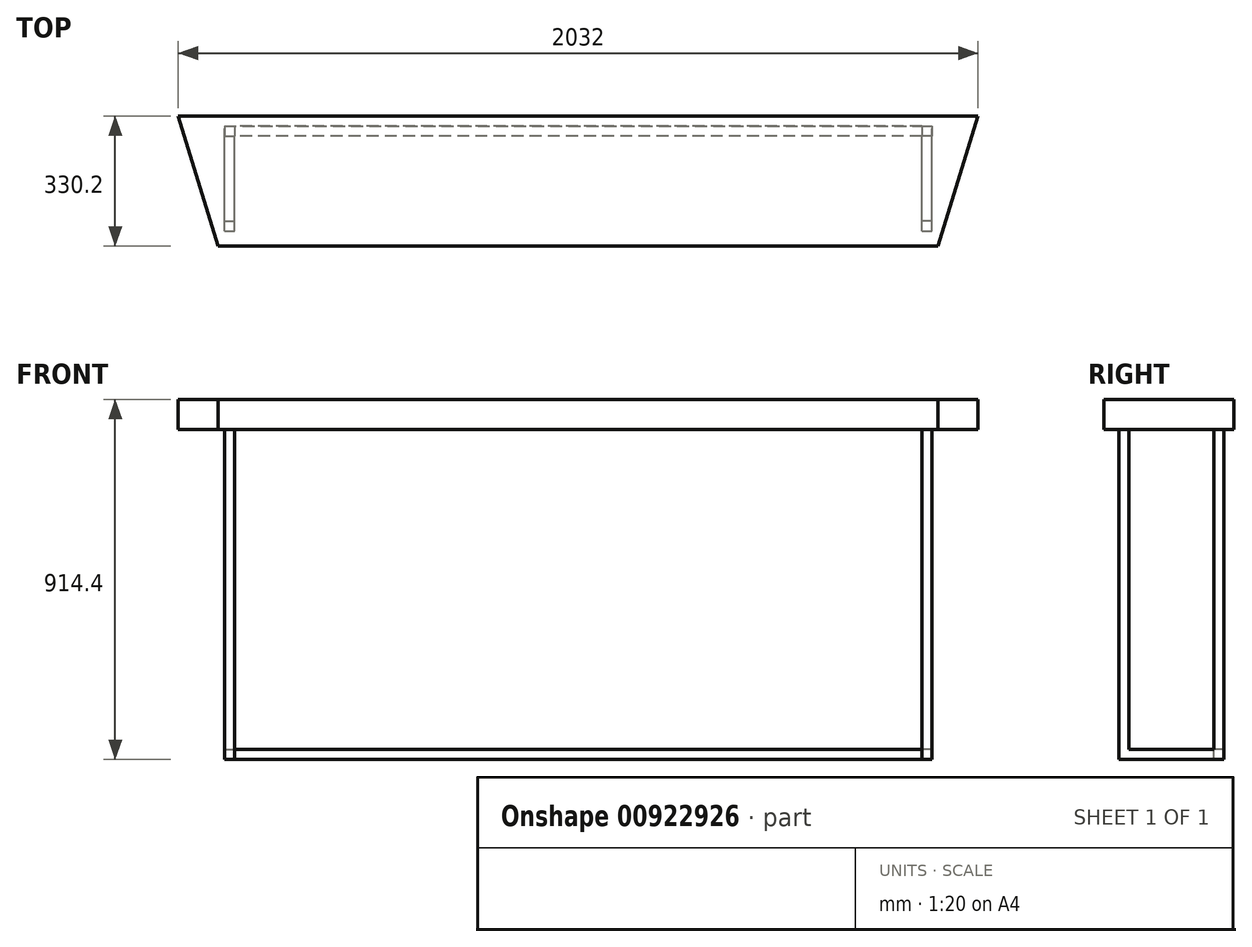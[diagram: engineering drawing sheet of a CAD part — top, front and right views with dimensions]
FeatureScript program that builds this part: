
annotation { "Feature Type Name" : "Feature", "Feature Type Description" : "" }
export const myFeature = defineFeature(function(context is Context, id is Id, definition is map)
    precondition{}
    {
        {
            var Q0;
            Q0=qCreatedBy(makeId("Top.planeOp"),FACE);
            var sketch = newSketch(context, id + "F0", { "sketchPlane" : qUnion([Q0])});
            skLineSegment(sketch, "E0.bottom", {"start": v(-914.4, 165.1) * mm, "end": v(914.4, 165.1) * mm});
            skLineSegment(sketch, "E0.top", {"start": v(-914.4, -165.1) * mm, "end": v(914.4, -165.1) * mm});
            skLineSegment(sketch, "E0.left", {"start": v(-914.4, 165.1) * mm, "end": v(-914.4, -165.1) * mm});
            skLineSegment(sketch, "E0.right", {"start": v(914.4, 165.1) * mm, "end": v(914.4, -165.1) * mm});
            skPoint(sketch, "E0.middle", {"position": v(0, 0) * mm});
            skLineSegment(sketch, "E1.bottom", {"start": v(-1016, 165.1) * mm, "end": v(1016, 165.1) * mm});
            skLineSegment(sketch, "E1.top", {"start": v(-1016, -165.1) * mm, "end": v(1016, -165.1) * mm});
            skLineSegment(sketch, "E1.left", {"start": v(-1016, 165.1) * mm, "end": v(-1016, -165.1) * mm});
            skLineSegment(sketch, "E1.right", {"start": v(1016, 165.1) * mm, "end": v(1016, -165.1) * mm});
            skLineSegment(sketch, "E2", {"start": v(-1016, 165.1) * mm, "end": v(-914.4, -165.1) * mm});
            skLineSegment(sketch, "E3", {"start": v(914.4, -165.1) * mm, "end": v(1016, 165.1) * mm});
            skSolve(sketch);
        }
        {
            var Q0;
            {var subQ0=sQuery(id+"F0.wireOp",EDGE,"E0.left");Q0=makeQuery(id+"F0.imprint","IMPRINT",FACE,{"disambiguationData":[TD([[makeQuery(id+"F0.imprint","IMPRINT",EDGE,{"derivedFrom":subQ0}),1.0]])]});}
            var Q1;
            {var subQ0=sQuery(id+"F0.wireOp",EDGE,"E0.left");Q1=makeQuery(id+"F0.imprint","IMPRINT",FACE,{"disambiguationData":[TD([[makeQuery(id+"F0.imprint","IMPRINT",EDGE,{"derivedFrom":subQ0}),-1.0]])]});}
            var Q2;
            {var subQ0=sQuery(id+"F0.wireOp",EDGE,"E0.right");Q2=makeQuery(id+"F0.imprint","IMPRINT",FACE,{"disambiguationData":[TD([[makeQuery(id+"F0.imprint","IMPRINT",EDGE,{"derivedFrom":subQ0}),1.0]])]});}
            extrude(context, id + "F1", {"entities" : qUnion([Q0, Q1, Q2]), "depth" : 76.2 * mm, "offsetDistance" : 25.4 * mm});
        }
        {
            var Q0;
            Q0=makeQuery(id+"F1.opExtrude","CAP_FACE",FACE,{"disambiguationData":[OSD([sQuery(id+"F0.wireOp",EDGE,"E1.bottom"),sQuery(id+"F0.wireOp",EDGE,"E1.top"),sQuery(id+"F0.wireOp",EDGE,"E2"),sQuery(id+"F0.wireOp",EDGE,"E3")])],"isStart":true});
            var sketch = newSketch(context, id + "F2", { "sketchPlane" : qUnion([Q0])});
            skLineSegment(sketch, "E4", {"start": v(-898.53, 127) * mm, "end": v(898.53, 127) * mm});
            skPoint(sketch, "E5", {"position": v(0, 127) * mm});
            skLineSegment(sketch, "E6.0", {"start": v(-898.52, -139.7) * mm, "end": v(898.53, -139.7) * mm});
            skLineSegment(sketch, "E7.bottom", {"start": v(-898.53, 127) * mm, "end": v(-873.13, 127) * mm});
            skLineSegment(sketch, "E7.top", {"start": v(-898.53, 101.6) * mm, "end": v(-873.13, 101.6) * mm});
            skLineSegment(sketch, "E7.left", {"start": v(-898.53, 127) * mm, "end": v(-898.53, 101.6) * mm});
            skLineSegment(sketch, "E7.right", {"start": v(-873.13, 127) * mm, "end": v(-873.13, 101.6) * mm});
            skLineSegment(sketch, "E8.bottom", {"start": v(-898.52, -139.7) * mm, "end": v(-873.12, -139.7) * mm});
            skLineSegment(sketch, "E8.top", {"start": v(-898.52, -114.3) * mm, "end": v(-873.12, -114.3) * mm});
            skLineSegment(sketch, "E8.left", {"start": v(-898.52, -139.7) * mm, "end": v(-898.52, -114.3) * mm});
            skLineSegment(sketch, "E8.right", {"start": v(-873.12, -139.7) * mm, "end": v(-873.12, -114.3) * mm});
            skLineSegment(sketch, "E9.bottom", {"start": v(898.53, 127) * mm, "end": v(873.13, 127) * mm});
            skLineSegment(sketch, "E9.top", {"start": v(898.53, 101.6) * mm, "end": v(873.13, 101.6) * mm});
            skLineSegment(sketch, "E9.left", {"start": v(898.53, 127) * mm, "end": v(898.53, 101.6) * mm});
            skLineSegment(sketch, "E9.right", {"start": v(873.13, 127) * mm, "end": v(873.13, 101.6) * mm});
            skLineSegment(sketch, "E10.bottom", {"start": v(898.53, -139.7) * mm, "end": v(873.13, -139.7) * mm});
            skLineSegment(sketch, "E10.top", {"start": v(898.53, -114.3) * mm, "end": v(873.13, -114.3) * mm});
            skLineSegment(sketch, "E10.left", {"start": v(898.53, -139.7) * mm, "end": v(898.53, -114.3) * mm});
            skLineSegment(sketch, "E10.right", {"start": v(873.13, -139.7) * mm, "end": v(873.13, -114.3) * mm});
            skSolve(sketch);
        }
        {
            var Q0;
            Q0 = qSketchRegion(id + "F2", true);
            extrude(context, id + "F3", {"entities" : qUnion([Q0]), "operationType" : NewBodyOperationType.ADD, "depth" : 838.2 * mm, "offsetDistance" : 25.4 * mm});
        }
        {
            var Q0;
            Q0=makeQuery(id+"F3.opExtrude","SWEPT_FACE",FACE,{"disambiguationData":[OSD([sQuery(id+"F2.wireOp",EDGE,"E8.right")])]});
            var sketch = newSketch(context, id + "F4", { "sketchPlane" : qUnion([Q0])});
            skLineSegment(sketch, "E11.0", {"start": v(114.3, -838.2) * mm, "end": v(114.3, 0) * mm});
            skLineSegment(sketch, "E12.0", {"start": v(139.7, -838.2) * mm, "end": v(139.7, 0) * mm});
            skLineSegment(sketch, "E13.0", {"start": v(139.7, -838.2) * mm, "end": v(114.3, -838.2) * mm});
            skLineSegment(sketch, "E14.0", {"start": v(139.7, -812.8) * mm, "end": v(114.3, -812.8) * mm});
            skSolve(sketch);
        }
        {
            var Q0;
            {var subQ0=sQuery(id+"F4.wireOp",EDGE,"E13.0");Q0=makeQuery(id+"F4.imprint","IMPRINT",FACE,{"disambiguationData":[TD([[makeQuery(id+"F4.imprint","IMPRINT",EDGE,{"derivedFrom":subQ0}),-1.0]])]});}
            extrude(context, id + "F5", {"entities" : qUnion([Q0]), "operationType" : NewBodyOperationType.ADD, "endBound" : BoundingType.UP_TO_NEXT, "depth" : 25.4 * mm, "offsetDistance" : 25.4 * mm});
        }
        {
            var Q0;
            Q0=makeQuery(id+"F5.boolean.opBoolean","MERGE",FACE,{"derivedFrom":[makeQuery(id+"F3.opExtrude","SWEPT_FACE",FACE,{"disambiguationData":[OSD([sQuery(id+"F2.wireOp",EDGE,"E8.top")])]}),makeQuery(id+"F3.opExtrude","SWEPT_FACE",FACE,{"disambiguationData":[OSD([sQuery(id+"F2.wireOp",EDGE,"E10.top")])]}),makeQuery(id+"F5.opExtrude","SWEPT_FACE",FACE,{"disambiguationData":[OSD([sQuery(id+"F4.wireOp",EDGE,"E11.0")])]})]});
            var sketch = newSketch(context, id + "F6", { "sketchPlane" : qUnion([Q0])});
            skLineSegment(sketch, "E15.bottom", {"start": v(873.13, -812.8) * mm, "end": v(898.53, -812.8) * mm});
            skLineSegment(sketch, "E15.top", {"start": v(873.13, -838.2) * mm, "end": v(898.53, -838.2) * mm});
            skLineSegment(sketch, "E15.left", {"start": v(873.13, -812.8) * mm, "end": v(873.13, -838.2) * mm});
            skLineSegment(sketch, "E15.right", {"start": v(898.53, -812.8) * mm, "end": v(898.53, -838.2) * mm});
            skLineSegment(sketch, "E16.bottom", {"start": v(-898.52, -838.2) * mm, "end": v(-873.12, -838.2) * mm});
            skLineSegment(sketch, "E16.top", {"start": v(-898.52, -812.8) * mm, "end": v(-873.12, -812.8) * mm});
            skLineSegment(sketch, "E16.left", {"start": v(-898.52, -838.2) * mm, "end": v(-898.52, -812.8) * mm});
            skLineSegment(sketch, "E16.right", {"start": v(-873.12, -838.2) * mm, "end": v(-873.12, -812.8) * mm});
            skSolve(sketch);
        }
        {
            var Q0;
            Q0 = qSketchRegion(id + "F6", true);
            extrude(context, id + "F7", {"entities" : qUnion([Q0]), "operationType" : NewBodyOperationType.ADD, "endBound" : BoundingType.UP_TO_NEXT, "depth" : 25.4 * mm, "offsetDistance" : 25.4 * mm});
        }
    });
